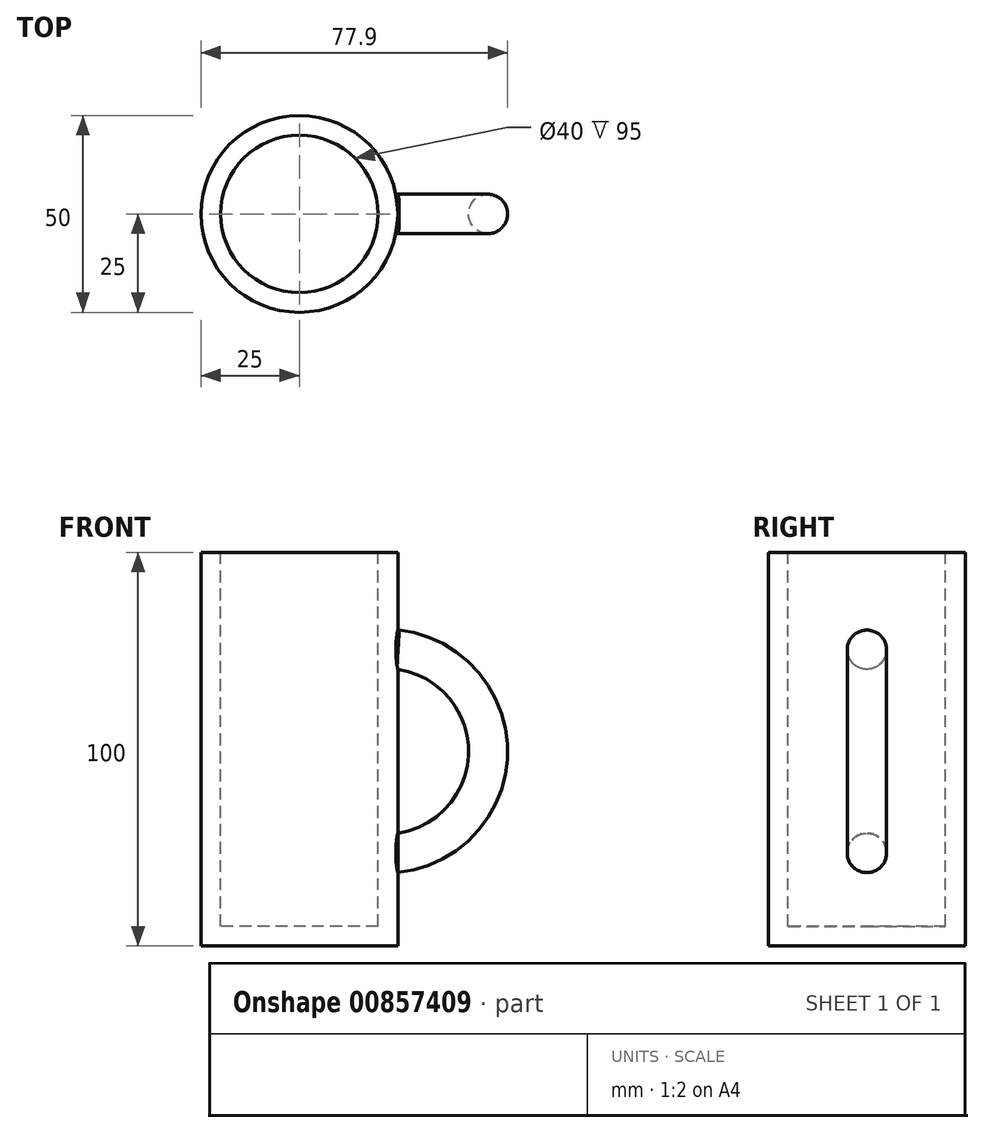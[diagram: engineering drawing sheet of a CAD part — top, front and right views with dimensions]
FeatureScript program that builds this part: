
annotation { "Feature Type Name" : "Feature", "Feature Type Description" : "" }
export const myFeature = defineFeature(function(context is Context, id is Id, definition is map)
    precondition{}
    {
        {
            var Q0;
            Q0=qCreatedBy(makeId("Top.planeOp"),FACE);
            var sketch = newSketch(context, id + "F0", { "sketchPlane" : qUnion([Q0])});
            skCircle(sketch, "E0", {"center": v(0, 0) * mm, "radius": 25 * mm});
            skSolve(sketch);
        }
        {
            var Q0;
            Q0=makeQuery(id+"F0.imprint","IMPRINT",FACE,{"disambiguationData":[TD([[makeQuery(id+"F0.imprint","IMPRINT",EDGE,{"derivedFrom":sQuery(id+"F0.wireOp",EDGE,"E0")}),1.0]])]});
            extrude(context, id + "F1", {"entities" : qUnion([Q0]), "depth" : 100 * mm, "offsetDistance" : 25 * mm});
        }
        {
            var Q0;
            Q0=makeQuery(id+"F1.opExtrude","CAP_FACE",FACE,{"disambiguationData":[OSD([sQuery(id+"F0.wireOp",EDGE,"E0")])],"isStart":false});
            var sketch = newSketch(context, id + "F2", { "sketchPlane" : qUnion([Q0])});
            skCircle(sketch, "E1", {"center": v(0, 0) * mm, "radius": 20 * mm});
            skSolve(sketch);
        }
        {
            var Q0;
            Q0=makeQuery(id+"F2.imprint","IMPRINT",FACE,{"disambiguationData":[TD([[makeQuery(id+"F2.imprint","IMPRINT",EDGE,{"derivedFrom":sQuery(id+"F2.wireOp",EDGE,"E1")}),1.0]])]});
            extrude(context, id + "F3", {"entities" : qUnion([Q0]), "operationType" : NewBodyOperationType.REMOVE, "oppositeDirection" : true, "depth" : 95 * mm, "offsetDistance" : 25 * mm});
        }
        {
            var Q0;
            Q0=qCreatedBy(makeId("Front.planeOp"),FACE);
            var sketch = newSketch(context, id + "F4", { "sketchPlane" : qUnion([Q0])});
            skArc(sketch, "E2", {"start": v(25.1, 23.36) * mm, "mid": v(48.23, 49.48) * mm, "end": v(25.08, 75.6) * mm});
            skLineSegment(sketch, "E3", {"start": v(25.08, 75.6) * mm, "end": v(23.86, 75.6) * mm});
            skLineSegment(sketch, "E4", {"start": v(25.1, 23.36) * mm, "end": v(23.5, 23.16) * mm});
            skSolve(sketch);
        }
        {
            var Q0;
            Q0=qCreatedBy(makeId("Right.planeOp"),FACE);
            cPlane(context, id + "F5", {"entities" : qUnion([Q0]), "cplaneType" : CPlaneType.OFFSET, "offset" : 25 * mm, "width" : 150 * mm, "height" : 150 * mm});
        }
        {
            var Q0;
            Q0=qCreatedBy(id+"F5.planeOp",FACE);
            var sketch = newSketch(context, id + "F6", { "sketchPlane" : qUnion([Q0])});
            skCircle(sketch, "E5", {"center": v(0, 23.64) * mm, "radius": 5 * mm});
            skSolve(sketch);
        }
        {
            var Q0;
            Q0=makeQuery(id+"F6.imprint","IMPRINT",FACE,{"disambiguationData":[TD([[makeQuery(id+"F6.imprint","IMPRINT",EDGE,{"derivedFrom":sQuery(id+"F6.wireOp",EDGE,"E5")}),1.0]])]});
            var Q1;
            Q1=sQuery(id+"F4.wireOp",EDGE,"E2");
            var Q2;
            Q2=sQuery(id+"F4.wireOp",EDGE,"E4");
            var Q3;
            Q3=sQuery(id+"F4.wireOp",EDGE,"E3");
            sweep(context, id + "F7", {"operationType" : NewBodyOperationType.ADD, "profiles" : qUnion([Q0]), "path" : qUnion([Q1, Q2, Q3])});
        }
    });
